FCSTD DOCUMENT  (FreeCAD 0.20R27936 (Git))
Label: Angle Sketch
License: All rights reserved
LicenseURL: http://en.wikipedia.org/wiki/All_rights_reserved
objects: Sketcher::SketchObject×1
note: 1 computed .brp shape members not serialized (recipe doc carries the construction recipe); baked Part::Feature solids carry a one-line shape summary decoded from their .brp

FEATURE [Sketcher::SketchObject] Sketch
  FullyConstrained = false
  sketch-geometry (23):
    g0: LineSegment StartX=43.1308 StartY=53.8476 StartZ=0 EndX=38.1308 EndY=40.1102 EndZ=0
    g1: LineSegment StartX=38.1308 StartY=40.1102 StartZ=0 EndX=48.1308 EndY=40.1102 EndZ=0
    g2: LineSegment StartX=48.1308 StartY=40.1102 StartZ=0 EndX=43.1308 EndY=53.8476 EndZ=0
    g3: LineSegment StartX=94.9407 StartY=62.4449 StartZ=0 EndX=89.9407 EndY=48.7075 EndZ=0
    g4: LineSegment StartX=89.9407 StartY=48.7075 StartZ=0 EndX=99.9407 EndY=48.7075 EndZ=0
    g5: LineSegment StartX=99.9407 StartY=48.7075 StartZ=0 EndX=94.9407 EndY=62.4449 EndZ=0
    g6: GeomPoint X=43.1308 Y=46.9789 Z=0
    g7: GeomPoint X=94.9407 Y=55.5762 Z=0
    g8: LineSegment StartX=43.1308 StartY=53.8476 StartZ=0 EndX=43.1308 EndY=40.1102 EndZ=0
    g9: LineSegment StartX=94.9407 StartY=62.4449 StartZ=0 EndX=94.9407 EndY=48.7075 EndZ=0
    g10: LineSegment StartX=94.9407 StartY=55.5762 StartZ=0 EndX=54.4846 EndY=0 EndZ=0
    g11: LineSegment StartX=94.9407 StartY=55.5762 StartZ=0 EndX=135.397 EndY=0 EndZ=0
    g12: LineSegment StartX=43.1308 StartY=46.9789 StartZ=0 EndX=77.3286 EndY=0 EndZ=0
    g13: LineSegment StartX=43.1308 StartY=46.9789 StartZ=0 EndX=8.93295 EndY=0 EndZ=0
    g14: LineSegment StartX=43.1308 StartY=46.9789 StartZ=0 EndX=43.1308 EndY=146.979 EndZ=0
    g15: LineSegment StartX=94.9407 StartY=55.5762 StartZ=0 EndX=94.9407 EndY=155.576 EndZ=0
    g16: LineSegment StartX=43.1308 StartY=46.9789 StartZ=0 EndX=94.9407 EndY=55.5762 EndZ=0
    g17: LineSegment StartX=38.1308 StartY=40.1102 StartZ=0 EndX=89.9407 EndY=48.7075 EndZ=0
    g18: LineSegment StartX=94.9407 StartY=93.2334 StartZ=0 EndX=67.4904 EndY=17.8142 EndZ=0
    g19: LineSegment StartX=43.1308 StartY=84.7147 StartZ=0 EndX=70.6002 EndY=9.2431 EndZ=0
    g20: LineSegment StartX=70.6002 StartY=9.2431 StartZ=0 EndX=15.6614 EndY=9.2431 EndZ=0
    g21: LineSegment StartX=67.4904 StartY=17.8142 StartZ=0 EndX=122.429 EndY=17.8142 EndZ=0
    g22: LineSegment StartX=15.6614 StartY=9.2431 StartZ=0 EndX=67.4716 EndY=17.8388 EndZ=0
  constraints (67):
    c: Coincident(g0,g1)
    c: Horizontal(g1)
    c: Coincident(g1,g2)
    c: Coincident(g2,g0)
    c: Coincident(g3,g4)
    c: Horizontal(g4)
    c: Coincident(g4,g5)
    c: Coincident(g5,g3)
    c: Equal(g3,g5)
    c: Equal(g5,g2)
    c: Equal(g2,g0)
    c: Angle(g0,g2) = 0.698132
    c: Equal(g4,g1)
    c: DistanceX(g6) = 43.1308
    c: DistanceY(g6) = 46.9789
    c: DistanceX(g7) = 94.9407
    c: DistanceY(g7) = 55.5762
    c: Coincident(g8,g0)
    c: PointOnObject(g8,g1)
    c: Vertical(g8)
    c: Coincident(g9,g3)
    c: PointOnObject(g9,g4)
    c: Vertical(g9)
    c: Symmetric(g3,g9,g7)
    c: Symmetric(g0,g8,g6)
    c: DistanceX(g1,g1) = 10
    c: Coincident(g10,g7)
    c: PointOnObject(g10,g-1)
    c: PointOnObject(g3,g10)
    c: Coincident(g11,g7)
    c: PointOnObject(g11,g-1)
    c: PointOnObject(g4,g11)
    c: Coincident(g12,g6)
    c: PointOnObject(g12,g-1)
    c: Coincident(g13,g6)
    c: PointOnObject(g13,g-1)
    c: PointOnObject(g0,g13)
    c: PointOnObject(g1,g12)
    c: Coincident(g14,g6)
    c: Vertical(g14)
    c: Coincident(g15,g7)
    c: Vertical(g15)
    c: Equal(g15,g14)
    c: DistanceY(g14,g14) = 100
    c: Coincident(g16,g6)
    c: Coincident(g16,g7)
    c: Distance(g16) = 52.5184
    c: Coincident(g17,g0)
    c: Coincident(g17,g3)
    c: Distance(g17) = 52.5184
    c: PointOnObject(g18,g15)
    c: PointOnObject(g19,g14)
    c: PointOnObject(g19,g12)
    c: Parallel(g2,g19)
    c: Parallel(g18,g3)
    c: Coincident(g20,g19)
    c: PointOnObject(g20,g13)
    c: Horizontal(g20)
    c: Coincident(g21,g18)
    c: PointOnObject(g21,g11)
    c: Horizontal(g21)
    c: Equal(g20,g21)
    c: Angle(g-1,g16) = 0.16444
    c: Coincident(g22,g20)
    c: PointOnObject(g22,g19)
    c: Equal(g22,g17)
    c: Angle(g20,g22) = 0.16441
